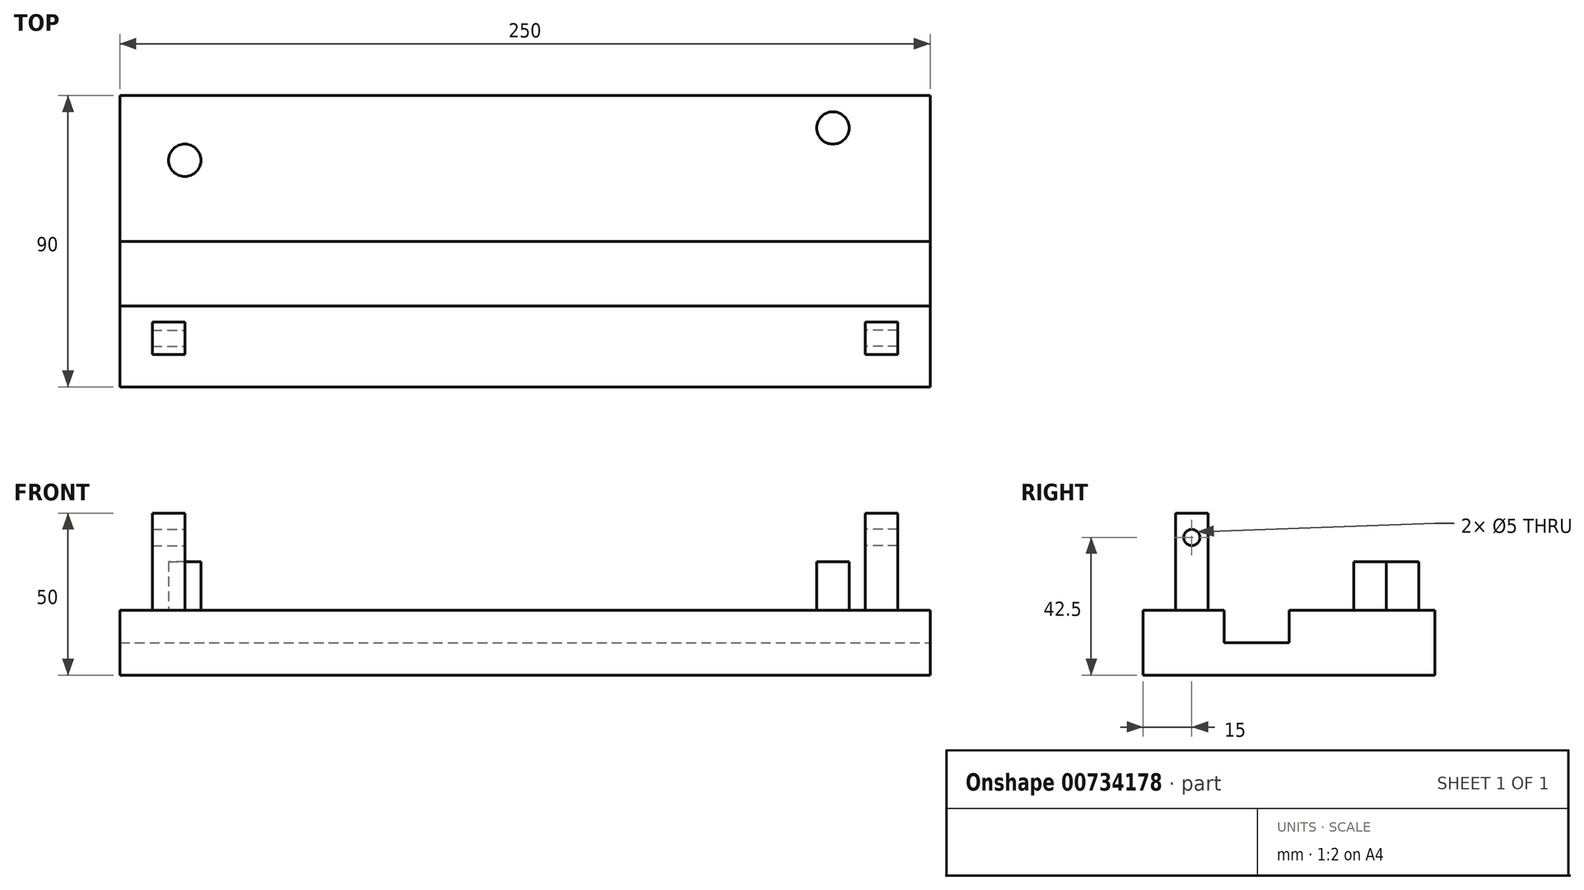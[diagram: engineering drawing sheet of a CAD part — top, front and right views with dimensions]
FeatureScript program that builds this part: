
annotation { "Feature Type Name" : "Feature", "Feature Type Description" : "" }
export const myFeature = defineFeature(function(context is Context, id is Id, definition is map)
    precondition{}
    {
        {
            var Q0;
            Q0=qCreatedBy(makeId("Top.planeOp"),FACE);
            var sketch = newSketch(context, id + "F0", { "sketchPlane" : qUnion([Q0])});
            skLineSegment(sketch, "E0.bottom", {"start": v(125, -45) * mm, "end": v(-125, -45) * mm});
            skLineSegment(sketch, "E0.top", {"start": v(125, 45) * mm, "end": v(-125, 45) * mm});
            skLineSegment(sketch, "E0.left", {"start": v(125, -45) * mm, "end": v(125, 45) * mm});
            skLineSegment(sketch, "E0.right", {"start": v(-125, -45) * mm, "end": v(-125, 45) * mm});
            skPoint(sketch, "E0.middle", {"position": v(0, 0) * mm});
            skSolve(sketch);
        }
        {
            var Q0;
            Q0 = qSketchRegion(id + "F0", true);
            extrude(context, id + "F1", {"entities" : qUnion([Q0]), "depth" : 20 * mm, "offsetDistance" : 25 * mm});
        }
        {
            var Q0;
            Q0=makeQuery(id+"F1.opExtrude","CAP_FACE",FACE,{"disambiguationData":[OSD([sQuery(id+"F0.wireOp",EDGE,"E0.bottom"),sQuery(id+"F0.wireOp",EDGE,"E0.top"),sQuery(id+"F0.wireOp",EDGE,"E0.left"),sQuery(id+"F0.wireOp",EDGE,"E0.right")])],"isStart":false});
            var sketch = newSketch(context, id + "F2", { "sketchPlane" : qUnion([Q0])});
            skCircle(sketch, "E1", {"center": v(95, 35) * mm, "radius": 5 * mm});
            skCircle(sketch, "E2", {"center": v(-105, 25) * mm, "radius": 5 * mm});
            skSolve(sketch);
        }
        {
            var Q0;
            Q0 = qSketchRegion(id + "F2", true);
            extrude(context, id + "F3", {"entities" : qUnion([Q0]), "operationType" : NewBodyOperationType.ADD, "depth" : 15 * mm, "offsetDistance" : 25 * mm});
        }
        {
            var Q0;
            Q0=makeQuery(id+"F1.opExtrude","CAP_FACE",FACE,{"disambiguationData":[OSD([sQuery(id+"F0.wireOp",EDGE,"E0.bottom"),sQuery(id+"F0.wireOp",EDGE,"E0.top"),sQuery(id+"F0.wireOp",EDGE,"E0.left"),sQuery(id+"F0.wireOp",EDGE,"E0.right")])],"isStart":false});
            var sketch = newSketch(context, id + "F4", { "sketchPlane" : qUnion([Q0])});
            skLineSegment(sketch, "E3.bottom", {"start": v(-125, 0) * mm, "end": v(125, 0) * mm});
            skLineSegment(sketch, "E3.top", {"start": v(-125, -20) * mm, "end": v(125, -20) * mm});
            skLineSegment(sketch, "E3.left", {"start": v(-125, 0) * mm, "end": v(-125, -20) * mm});
            skLineSegment(sketch, "E3.right", {"start": v(125, 0) * mm, "end": v(125, -20) * mm});
            skSolve(sketch);
        }
        {
            var Q0;
            Q0 = qSketchRegion(id + "F4", true);
            extrude(context, id + "F5", {"entities" : qUnion([Q0]), "operationType" : NewBodyOperationType.REMOVE, "oppositeDirection" : true, "depth" : 10 * mm, "offsetDistance" : 25 * mm});
        }
        {
            var Q0;
            {var subQ0=sQuery(id+"F0.wireOp",EDGE,"E0.bottom");var subQ1=sQuery(id+"F0.wireOp",EDGE,"E0.right");var subQ2=sQuery(id+"F0.wireOp",EDGE,"E0.left");Q0=makeQuery(id+"F5.boolean.opBoolean","SPLIT",FACE,{"disambiguationData":[TD([makeQuery(id+"F1.opExtrude","SWEPT_FACE",FACE,{"disambiguationData":[OSD([subQ0])]})])],"derivedFrom":makeQuery(id+"F1.opExtrude","CAP_FACE",FACE,{"disambiguationData":[OSD([subQ0,sQuery(id+"F0.wireOp",EDGE,"E0.top"),subQ2,subQ1])],"isStart":false})});}
            var sketch = newSketch(context, id + "F6", { "sketchPlane" : qUnion([Q0])});
            skLineSegment(sketch, "E4.bottom", {"start": v(-115, -35) * mm, "end": v(-105, -35) * mm});
            skLineSegment(sketch, "E4.top", {"start": v(-115, -25) * mm, "end": v(-105, -25) * mm});
            skLineSegment(sketch, "E4.left", {"start": v(-115, -35) * mm, "end": v(-115, -25) * mm});
            skLineSegment(sketch, "E4.right", {"start": v(-105, -35) * mm, "end": v(-105, -25) * mm});
            skLineSegment(sketch, "E5.MirrorCS", {"start": v(115, -35) * mm, "end": v(105, -35) * mm});
            skLineSegment(sketch, "E6.MirrorCS", {"start": v(105, -35) * mm, "end": v(105, -25) * mm});
            skLineSegment(sketch, "E7.MirrorCS", {"start": v(115, -25) * mm, "end": v(105, -25) * mm});
            skLineSegment(sketch, "E8.MirrorCS", {"start": v(115, -35) * mm, "end": v(115, -25) * mm});
            skSolve(sketch);
        }
        {
            var Q0;
            Q0 = qSketchRegion(id + "F6", true);
            extrude(context, id + "F7", {"entities" : qUnion([Q0]), "operationType" : NewBodyOperationType.ADD, "depth" : 30 * mm, "offsetDistance" : 25 * mm});
        }
        {
            var Q0;
            Q0=makeQuery(id+"F7.opExtrude","SWEPT_FACE",FACE,{"disambiguationData":[OSD([sQuery(id+"F6.wireOp",EDGE,"E4.right")])]});
            var sketch = newSketch(context, id + "F8", { "sketchPlane" : qUnion([Q0])});
            skPoint(sketch, "E9.centerSnap0", {"position": v(-35, 35) * mm});
            skCircle(sketch, "E10", {"center": v(-30, 42.5) * mm, "radius": 2.5 * mm});
            skSolve(sketch);
        }
        {
            var Q0;
            Q0 = qSketchRegion(id + "F8", true);
            extrude(context, id + "F9", {"entities" : qUnion([Q0]), "operationType" : NewBodyOperationType.REMOVE, "endBound" : BoundingType.THROUGH_ALL, "oppositeDirection" : true, "depth" : 25 * mm, "offsetDistance" : 25 * mm});
        }
        {
            var Q0;
            Q0=makeQuery(id+"F7.opExtrude","SWEPT_FACE",FACE,{"disambiguationData":[OSD([sQuery(id+"F6.wireOp",EDGE,"E6.MirrorCS")])]});
            var sketch = newSketch(context, id + "F10", { "sketchPlane" : qUnion([Q0])});
            skPoint(sketch, "E11.centerSnap0", {"position": v(30, 50) * mm});
            skPoint(sketch, "E11.centerSnap1", {"position": v(25, 35) * mm});
            skCircle(sketch, "E12", {"center": v(30, 42.5) * mm, "radius": 2.5 * mm});
            skSolve(sketch);
        }
        {
            var Q0;
            Q0 = qSketchRegion(id + "F10", true);
            extrude(context, id + "F11", {"entities" : qUnion([Q0]), "operationType" : NewBodyOperationType.REMOVE, "endBound" : BoundingType.THROUGH_ALL, "oppositeDirection" : true, "depth" : 25 * mm, "offsetDistance" : 25 * mm});
        }
    });
